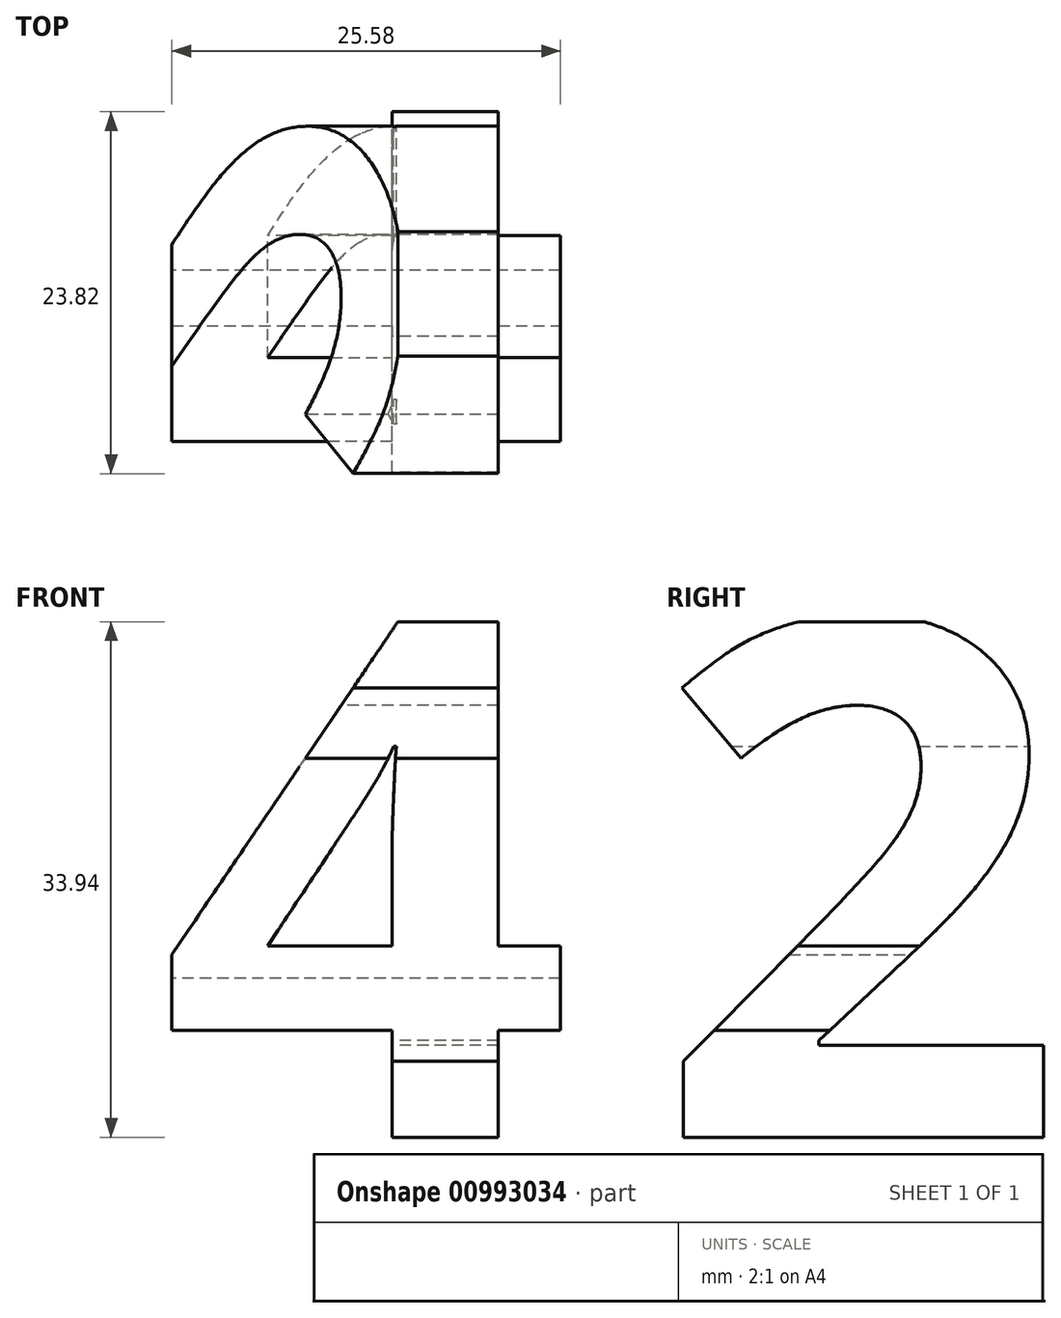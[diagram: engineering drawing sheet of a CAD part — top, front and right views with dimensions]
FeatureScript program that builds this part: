
annotation { "Feature Type Name" : "Feature", "Feature Type Description" : "" }
export const myFeature = defineFeature(function(context is Context, id is Id, definition is map)
    precondition{}
    {
        {
            var Q0;
            Q0=qCreatedBy(makeId("Front.planeOp"),FACE);
            var sketch = newSketch(context, id + "F0", { "sketchPlane" : qUnion([Q0])});
            skLineSegment(sketch, "E0.bottom", {"start": v(0, 34.42) * mm, "end": v(19.9, 34.42) * mm});
            skLineSegment(sketch, "E0.top", {"start": v(0, 0) * mm, "end": v(19.9, 0) * mm});
            skLineSegment(sketch, "E0.left", {"start": v(0, 34.42) * mm, "end": v(0, 0) * mm});
            skLineSegment(sketch, "E0.right", {"start": v(19.9, 34.42) * mm, "end": v(19.9, 0) * mm});
            skSolve(sketch);
        }
        {
            var Q0;
            Q0=makeQuery(id+"F0.imprint","IMPRINT",FACE,{"disambiguationData":[TD([[makeQuery(id+"F0.imprint","IMPRINT",EDGE,{"derivedFrom":sQuery(id+"F0.wireOp",EDGE,"E0.bottom")}),-1.0]])]});
            var Q1;
            Q1=sQuery(id+"F0.wireOp",EDGE,"E0.left");
            revolve(context, id + "F1", {"surfaceOperationType" : NewSurfaceOperationType.NEW, "entities" : qUnion([Q0]), "axis" : qUnion([Q1]), "revolveType" : RevolveType.FULL});
        }
        {
            var Q0;
            Q0=qCreatedBy(makeId("Front.planeOp"),FACE);
            var sketch = newSketch(context, id + "F2", { "sketchPlane" : qUnion([Q0])});
            skText(sketch, "E1", { "text": "4", "fontName": "OpenSans-Bold.ttf"});
            const initialGuessF2  = {"E1": [-0.01498, 0, 1, 0, 0.03423]};
            skSetInitialGuess(sketch, initialGuessF2);
            skSolve(sketch);
        }
        {
            var Q0;
            Q0 = qSketchRegion(id + "F2", true);
            extrude(context, id + "F3", {"entities" : qUnion([Q0]), "operationType" : NewBodyOperationType.INTERSECT, "endBound" : BoundingType.SYMMETRIC, "depth" : 83.4 * mm, "offsetDistance" : 25 * mm});
        }
        {
            var Q0;
            Q0=qCreatedBy(makeId("Right.planeOp"),FACE);
            var sketch = newSketch(context, id + "F4", { "sketchPlane" : qUnion([Q0])});
            skText(sketch, "E2", { "text": "2", "fontName": "OpenSans-Bold.ttf"});
            const initialGuessF4  = {"E2": [-0.01413, 0, 1, 0, 0.03423]};
            skSetInitialGuess(sketch, initialGuessF4);
            skSolve(sketch);
        }
        {
            var Q0;
            Q0 = qSketchRegion(id + "F4", true);
            extrude(context, id + "F5", {"entities" : qUnion([Q0]), "operationType" : NewBodyOperationType.INTERSECT, "endBound" : BoundingType.SYMMETRIC, "depth" : 61.8 * mm, "offsetDistance" : 25 * mm});
        }
    });
